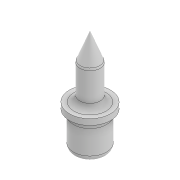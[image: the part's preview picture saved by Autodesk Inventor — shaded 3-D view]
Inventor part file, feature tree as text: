
AUTODESK INVENTOR PART (.ipt)
format: ipt  version: 2022 (Build 260153000, 153)  size: 262,144 bytes
history: native  units: mm
features: sketch x3, extrude x2, fillet x2, revolve x1, projected_geometry x1
ambient origin geometry x8: Origin, YZ Plane, XZ Plane, XY Plane, X Axis, Y Axis, Z Axis, Center Point
bodies: Solid1 (feature_tree)
feature tree (9):
  extrude  "Extrusion1"  Depth=12.0mm TaperAngle=0.0deg
  fillet  "Fillet1"  Radius=2.0mm
  extrude  "Extrusion2"  Depth=2.0mm TaperAngle=0.0deg
  revolve  "Revolution1"  [1 undecoded]
  fillet  "Fillet2"  [1 undecoded]
  sketch  "Sketch1"  dims[d0=11.2mm d1=12.0mm d2=0.0mm d3=2.0mm]
  sketch  "Sketch2"  dims[d4=14.0mm d5=2.0mm d6=0.0mm]
  sketch  "Sketch3"  dims[d7=21.0mm d8=3.665191mm d9=90.0deg d10=2.0mm]
  projected_geometry  "Projected Loop1"
note: 2 required parameter values undecoded (feature->parameter linkage not recoverable at this tier; creation-order binding heuristic only, values carry confidence <= 0.55)